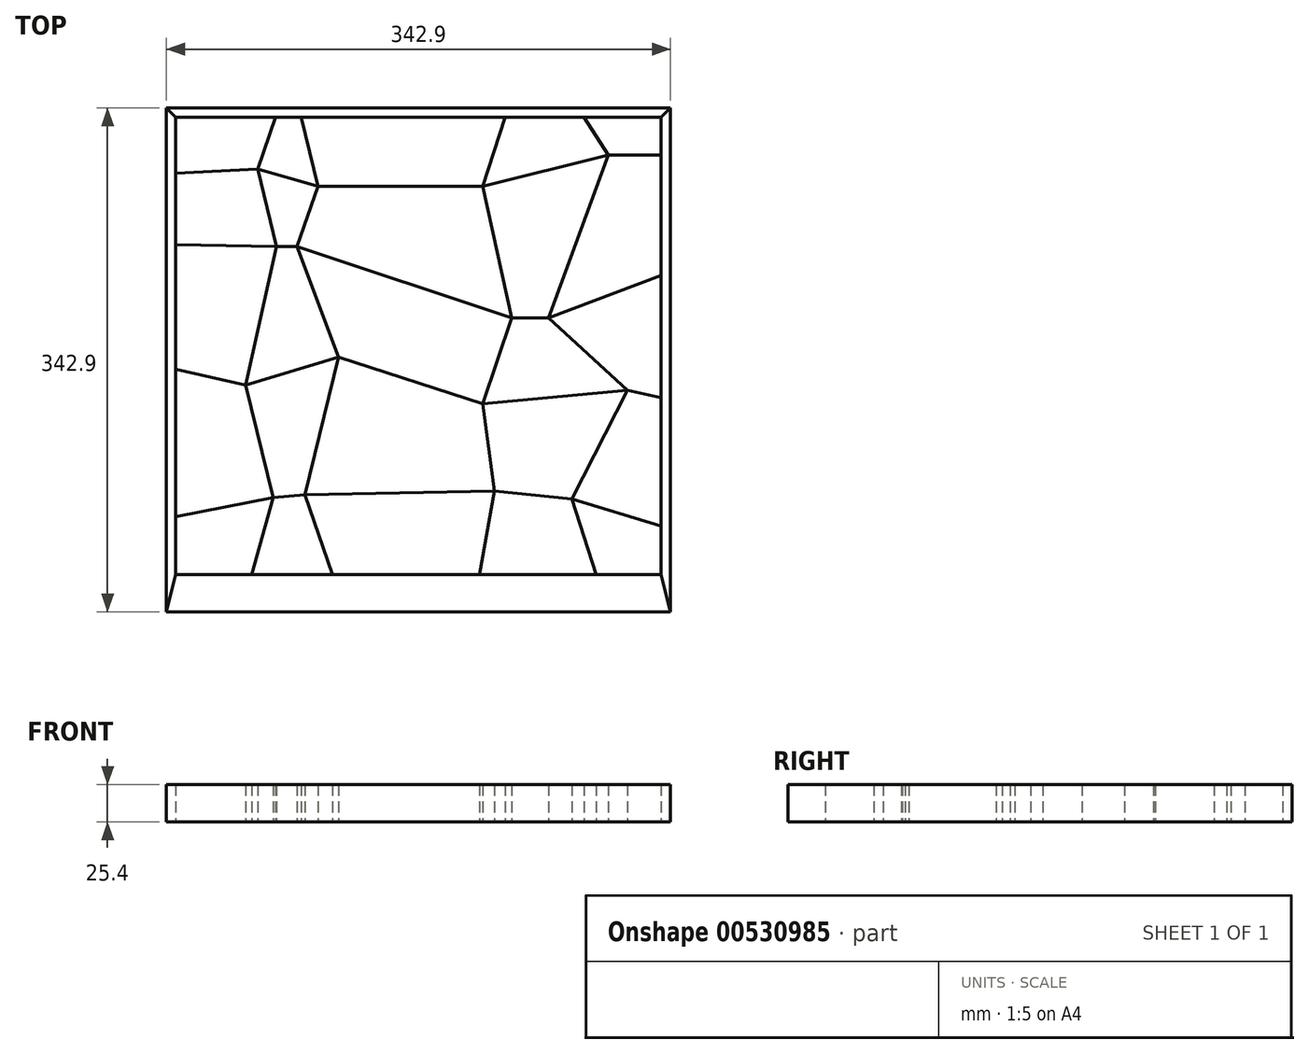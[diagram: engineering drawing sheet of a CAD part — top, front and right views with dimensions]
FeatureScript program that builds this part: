
annotation { "Feature Type Name" : "Feature", "Feature Type Description" : "" }
export const myFeature = defineFeature(function(context is Context, id is Id, definition is map)
    precondition{}
    {
        {
            var Q0;
            Q0=qCreatedBy(makeId("Top.planeOp"),FACE);
            var sketch = newSketch(context, id + "F0", { "sketchPlane" : qUnion([Q0])});
            skLineSegment(sketch, "E0.bottom", {"start": v(171.45, 171.45) * mm, "end": v(-171.45, 171.45) * mm});
            skLineSegment(sketch, "E0.top", {"start": v(171.45, -171.45) * mm, "end": v(-171.45, -171.45) * mm});
            skLineSegment(sketch, "E0.left", {"start": v(171.45, 171.45) * mm, "end": v(171.45, -171.45) * mm});
            skLineSegment(sketch, "E0.right", {"start": v(-171.45, 171.45) * mm, "end": v(-171.45, -171.45) * mm});
            skPoint(sketch, "E0.middle", {"position": v(0, 0) * mm});
            skLineSegment(sketch, "E1.bottom", {"start": v(165.1, 165.1) * mm, "end": v(-165.1, 165.1) * mm});
            skLineSegment(sketch, "E1.top", {"start": v(165.1, -146.05) * mm, "end": v(-165.1, -146.05) * mm});
            skLineSegment(sketch, "E1.left", {"start": v(165.1, 165.1) * mm, "end": v(165.1, -146.05) * mm});
            skLineSegment(sketch, "E1.right", {"start": v(-165.1, 165.1) * mm, "end": v(-165.1, -146.05) * mm});
            skPoint(sketch, "E1.middle", {"position": v(0, 9.53) * mm});
            skLineSegment(sketch, "E2", {"start": v(-165.1, 126.86) * mm, "end": v(-109.46, 129.92) * mm});
            skLineSegment(sketch, "E3", {"start": v(-109.46, 129.92) * mm, "end": v(-96.6, 76.98) * mm});
            skLineSegment(sketch, "E4", {"start": v(-96.6, 76.98) * mm, "end": v(-82.77, 76.98) * mm});
            skLineSegment(sketch, "E5", {"start": v(-82.77, 76.98) * mm, "end": v(-68.32, 118.21) * mm});
            skLineSegment(sketch, "E6", {"start": v(-68.32, 118.21) * mm, "end": v(43.61, 118.21) * mm});
            skLineSegment(sketch, "E7", {"start": v(43.61, 118.21) * mm, "end": v(63.29, 28.59) * mm});
            skLineSegment(sketch, "E8", {"start": v(63.29, 28.59) * mm, "end": v(88.64, 28.59) * mm});
            skLineSegment(sketch, "E9", {"start": v(88.64, 28.59) * mm, "end": v(129.05, 139.32) * mm});
            skLineSegment(sketch, "E10", {"start": v(129.05, 139.32) * mm, "end": v(165.1, 139.32) * mm});
            skLineSegment(sketch, "E11", {"start": v(-109.46, 129.92) * mm, "end": v(-68.32, 118.21) * mm});
            skLineSegment(sketch, "E12", {"start": v(43.61, 118.21) * mm, "end": v(129.05, 139.32) * mm});
            skLineSegment(sketch, "E13", {"start": v(-68.32, 118.21) * mm, "end": v(-79.7, 165.1) * mm});
            skLineSegment(sketch, "E14", {"start": v(-109.46, 129.92) * mm, "end": v(-97.13, 165.1) * mm});
            skLineSegment(sketch, "E15", {"start": v(43.61, 118.21) * mm, "end": v(58.92, 165.1) * mm});
            skLineSegment(sketch, "E16", {"start": v(129.05, 139.32) * mm, "end": v(112.69, 165.1) * mm});
            skLineSegment(sketch, "E17", {"start": v(-165.1, 78.24) * mm, "end": v(-96.6, 76.98) * mm});
            skLineSegment(sketch, "E18", {"start": v(-82.77, 76.98) * mm, "end": v(63.29, 28.59) * mm});
            skLineSegment(sketch, "E19", {"start": v(88.64, 28.59) * mm, "end": v(165.1, 57.3) * mm});
            skLineSegment(sketch, "E20", {"start": v(63.29, 28.59) * mm, "end": v(43.9, -29.94) * mm});
            skLineSegment(sketch, "E21", {"start": v(88.64, 28.59) * mm, "end": v(142.3, -20.55) * mm});
            skLineSegment(sketch, "E22", {"start": v(-82.77, 76.98) * mm, "end": v(-54.36, 1.97) * mm});
            skLineSegment(sketch, "E23", {"start": v(-96.6, 76.98) * mm, "end": v(-117.68, -17.1) * mm});
            skLineSegment(sketch, "E24", {"start": v(-117.68, -17.1) * mm, "end": v(-54.36, 1.97) * mm});
            skLineSegment(sketch, "E25", {"start": v(-54.36, 1.97) * mm, "end": v(43.9, -29.94) * mm});
            skLineSegment(sketch, "E26", {"start": v(43.9, -29.94) * mm, "end": v(142.3, -20.55) * mm});
            skLineSegment(sketch, "E27", {"start": v(142.3, -20.55) * mm, "end": v(165.1, -25.65) * mm});
            skLineSegment(sketch, "E28", {"start": v(-117.68, -17.1) * mm, "end": v(-165.1, -6.49) * mm});
            skLineSegment(sketch, "E29", {"start": v(-117.68, -17.1) * mm, "end": v(-98.74, -93.65) * mm});
            skLineSegment(sketch, "E30", {"start": v(-54.36, 1.97) * mm, "end": v(-77.24, -91.93) * mm});
            skLineSegment(sketch, "E31", {"start": v(43.9, -29.94) * mm, "end": v(51.77, -89.35) * mm});
            skLineSegment(sketch, "E32", {"start": v(142.3, -20.55) * mm, "end": v(104.24, -94.5) * mm});
            skLineSegment(sketch, "E33", {"start": v(-165.1, -106.88) * mm, "end": v(-98.74, -93.65) * mm});
            skLineSegment(sketch, "E34", {"start": v(-98.74, -93.65) * mm, "end": v(-77.24, -91.93) * mm});
            skLineSegment(sketch, "E35", {"start": v(-77.24, -91.93) * mm, "end": v(51.77, -89.35) * mm});
            skLineSegment(sketch, "E36", {"start": v(51.77, -89.35) * mm, "end": v(104.24, -94.5) * mm});
            skLineSegment(sketch, "E37", {"start": v(104.24, -94.5) * mm, "end": v(165.1, -113.22) * mm});
            skLineSegment(sketch, "E38", {"start": v(-98.74, -93.65) * mm, "end": v(-113.3, -146.05) * mm});
            skLineSegment(sketch, "E39", {"start": v(-77.24, -91.93) * mm, "end": v(-58.53, -146.05) * mm});
            skLineSegment(sketch, "E40", {"start": v(51.77, -89.35) * mm, "end": v(41.57, -146.05) * mm});
            skLineSegment(sketch, "E41", {"start": v(104.24, -94.5) * mm, "end": v(120.92, -146.05) * mm});
            skLineSegment(sketch, "E42", {"start": v(-171.45, 171.45) * mm, "end": v(-165.1, 165.1) * mm});
            skLineSegment(sketch, "E43", {"start": v(171.45, 171.45) * mm, "end": v(165.1, 165.1) * mm});
            skLineSegment(sketch, "E44", {"start": v(-165.1, -146.05) * mm, "end": v(-171.45, -171.45) * mm});
            skLineSegment(sketch, "E45", {"start": v(165.1, -146.05) * mm, "end": v(171.45, -171.45) * mm});
            skSolve(sketch);
        }
        {
            var Q0;
            Q0=makeQuery(id+"F0.imprint","IMPRINT",FACE,{"disambiguationData":[TD([[makeQuery(id+"F0.imprint","IMPRINT",EDGE,{"derivedFrom":sQuery(id+"F0.wireOp",EDGE,"E0.bottom")}),1.0]])]});
            var Q1;
            Q1=makeQuery(id+"F0.imprint","IMPRINT",FACE,{"disambiguationData":[TD([[makeQuery(id+"F0.imprint","IMPRINT",EDGE,{"derivedFrom":sQuery(id+"F0.wireOp",EDGE,"E0.top")}),-1.0]])]});
            extrude(context, id + "F1", {"entities" : qUnion([Q0, Q1]), "depth" : 25.4 * mm, "offsetDistance" : 25.4 * mm});
        }
        {
            var Q0;
            Q0=makeQuery(id+"F0.imprint","IMPRINT",FACE,{"disambiguationData":[TD([[makeQuery(id+"F0.imprint","IMPRINT",EDGE,{"derivedFrom":sQuery(id+"F0.wireOp",EDGE,"E0.right")}),1.0]])]});
            var Q1;
            Q1=makeQuery(id+"F0.imprint","IMPRINT",FACE,{"disambiguationData":[TD([[makeQuery(id+"F0.imprint","IMPRINT",EDGE,{"derivedFrom":sQuery(id+"F0.wireOp",EDGE,"E0.left")}),-1.0]])]});
            extrude(context, id + "F2", {"entities" : qUnion([Q0, Q1]), "depth" : 25.4 * mm, "offsetDistance" : 25.4 * mm});
        }
        {
            var Q0;
            Q0=makeQuery(id+"F0.imprint","IMPRINT",FACE,{"disambiguationData":[TD([[makeQuery(id+"F0.imprint","IMPRINT",EDGE,{"derivedFrom":sQuery(id+"F0.wireOp",EDGE,"E11")}),1.0]])]});
            var Q1;
            Q1=makeQuery(id+"F0.imprint","IMPRINT",FACE,{"disambiguationData":[TD([[makeQuery(id+"F0.imprint","IMPRINT",EDGE,{"derivedFrom":sQuery(id+"F0.wireOp",EDGE,"E4")}),-1.0]])]});
            var Q2;
            Q2=makeQuery(id+"F0.imprint","IMPRINT",FACE,{"disambiguationData":[TD([[makeQuery(id+"F0.imprint","IMPRINT",EDGE,{"derivedFrom":sQuery(id+"F0.wireOp",EDGE,"E34")}),-1.0]])]});
            var Q3;
            Q3=makeQuery(id+"F0.imprint","IMPRINT",FACE,{"disambiguationData":[TD([[makeQuery(id+"F0.imprint","IMPRINT",EDGE,{"derivedFrom":sQuery(id+"F0.wireOp",EDGE,"E12")}),1.0]])]});
            var Q4;
            Q4=makeQuery(id+"F0.imprint","IMPRINT",FACE,{"disambiguationData":[TD([[makeQuery(id+"F0.imprint","IMPRINT",EDGE,{"derivedFrom":sQuery(id+"F0.wireOp",EDGE,"E8")}),-1.0]])]});
            var Q5;
            Q5=makeQuery(id+"F0.imprint","IMPRINT",FACE,{"disambiguationData":[TD([[makeQuery(id+"F0.imprint","IMPRINT",EDGE,{"derivedFrom":sQuery(id+"F0.wireOp",EDGE,"E36")}),-1.0]])]});
            extrude(context, id + "F3", {"entities" : qUnion([Q0, Q1, Q2, Q3, Q4, Q5]), "depth" : 25.4 * mm, "offsetDistance" : 25.4 * mm});
        }
        {
            var Q0;
            Q0=makeQuery(id+"F0.imprint","IMPRINT",FACE,{"disambiguationData":[TD([[makeQuery(id+"F0.imprint","IMPRINT",EDGE,{"derivedFrom":sQuery(id+"F0.wireOp",EDGE,"E3")}),1.0]])]});
            var Q1;
            Q1=makeQuery(id+"F0.imprint","IMPRINT",FACE,{"disambiguationData":[TD([[makeQuery(id+"F0.imprint","IMPRINT",EDGE,{"derivedFrom":sQuery(id+"F0.wireOp",EDGE,"E24")}),-1.0]])]});
            var Q2;
            Q2=makeQuery(id+"F0.imprint","IMPRINT",FACE,{"disambiguationData":[TD([[makeQuery(id+"F0.imprint","IMPRINT",EDGE,{"derivedFrom":sQuery(id+"F0.wireOp",EDGE,"E26")}),-1.0]])]});
            var Q3;
            Q3=makeQuery(id+"F0.imprint","IMPRINT",FACE,{"disambiguationData":[TD([[makeQuery(id+"F0.imprint","IMPRINT",EDGE,{"derivedFrom":sQuery(id+"F0.wireOp",EDGE,"E7")}),1.0]])]});
            var Q4;
            Q4=makeQuery(id+"F0.imprint","IMPRINT",FACE,{"disambiguationData":[TD([[makeQuery(id+"F0.imprint","IMPRINT",EDGE,{"derivedFrom":sQuery(id+"F0.wireOp",EDGE,"E6")}),1.0]])]});
            var Q5;
            {var subQ4=sQuery(id+"F0.wireOp",EDGE,"E2");Q5=makeQuery(id+"F0.imprint","IMPRINT",FACE,{"disambiguationData":[TD([[makeQuery(id+"F0.imprint","IMPRINT",EDGE,{"derivedFrom":subQ4}),1.0]])]});}
            var Q6;
            Q6=makeQuery(id+"F0.imprint","IMPRINT",FACE,{"disambiguationData":[TD([[makeQuery(id+"F0.imprint","IMPRINT",EDGE,{"derivedFrom":sQuery(id+"F0.wireOp",EDGE,"E18")}),-1.0]])]});
            var Q7;
            {var subQ0=sQuery(id+"F0.wireOp",EDGE,"E19");Q7=makeQuery(id+"F0.imprint","IMPRINT",FACE,{"disambiguationData":[TD([[makeQuery(id+"F0.imprint","IMPRINT",EDGE,{"derivedFrom":subQ0}),-1.0]])]});}
            var Q8;
            {var subQ4=sQuery(id+"F0.wireOp",EDGE,"E10");Q8=makeQuery(id+"F0.imprint","IMPRINT",FACE,{"disambiguationData":[TD([[makeQuery(id+"F0.imprint","IMPRINT",EDGE,{"derivedFrom":subQ4}),1.0]])]});}
            var Q9;
            {var subQ4=sQuery(id+"F0.wireOp",EDGE,"E37");Q9=makeQuery(id+"F0.imprint","IMPRINT",FACE,{"disambiguationData":[TD([[makeQuery(id+"F0.imprint","IMPRINT",EDGE,{"derivedFrom":subQ4}),-1.0]])]});}
            var Q10;
            Q10=makeQuery(id+"F0.imprint","IMPRINT",FACE,{"disambiguationData":[TD([[makeQuery(id+"F0.imprint","IMPRINT",EDGE,{"derivedFrom":sQuery(id+"F0.wireOp",EDGE,"E35")}),-1.0]])]});
            var Q11;
            {var subQ0=sQuery(id+"F0.wireOp",EDGE,"E17");Q11=makeQuery(id+"F0.imprint","IMPRINT",FACE,{"disambiguationData":[TD([[makeQuery(id+"F0.imprint","IMPRINT",EDGE,{"derivedFrom":subQ0}),-1.0]])]});}
            var Q12;
            {var subQ4=sQuery(id+"F0.wireOp",EDGE,"E33");Q12=makeQuery(id+"F0.imprint","IMPRINT",FACE,{"disambiguationData":[TD([[makeQuery(id+"F0.imprint","IMPRINT",EDGE,{"derivedFrom":subQ4}),-1.0]])]});}
            extrude(context, id + "F4", {"entities" : qUnion([Q0, Q1, Q2, Q3, Q4, Q5, Q6, Q7, Q8, Q9, Q10, Q11, Q12]), "depth" : 25.4 * mm, "offsetDistance" : 25.4 * mm});
        }
        {
            var Q0;
            {var subQ0=sQuery(id+"F0.wireOp",EDGE,"E2");Q0=makeQuery(id+"F0.imprint","IMPRINT",FACE,{"disambiguationData":[TD([[makeQuery(id+"F0.imprint","IMPRINT",EDGE,{"derivedFrom":subQ0}),-1.0]])]});}
            var Q1;
            Q1=makeQuery(id+"F0.imprint","IMPRINT",FACE,{"disambiguationData":[TD([[makeQuery(id+"F0.imprint","IMPRINT",EDGE,{"derivedFrom":sQuery(id+"F0.wireOp",EDGE,"E5")}),-1.0]])]});
            var Q2;
            Q2=makeQuery(id+"F0.imprint","IMPRINT",FACE,{"disambiguationData":[TD([[makeQuery(id+"F0.imprint","IMPRINT",EDGE,{"derivedFrom":sQuery(id+"F0.wireOp",EDGE,"E9")}),-1.0]])]});
            var Q3;
            {var subQ0=sQuery(id+"F0.wireOp",EDGE,"E27");Q3=makeQuery(id+"F0.imprint","IMPRINT",FACE,{"disambiguationData":[TD([[makeQuery(id+"F0.imprint","IMPRINT",EDGE,{"derivedFrom":subQ0}),-1.0]])]});}
            var Q4;
            Q4=makeQuery(id+"F0.imprint","IMPRINT",FACE,{"disambiguationData":[TD([[makeQuery(id+"F0.imprint","IMPRINT",EDGE,{"derivedFrom":sQuery(id+"F0.wireOp",EDGE,"E25")}),-1.0]])]});
            var Q5;
            {var subQ0=sQuery(id+"F0.wireOp",EDGE,"E28");Q5=makeQuery(id+"F0.imprint","IMPRINT",FACE,{"disambiguationData":[TD([[makeQuery(id+"F0.imprint","IMPRINT",EDGE,{"derivedFrom":subQ0}),1.0]])]});}
            extrude(context, id + "F5", {"entities" : qUnion([Q0, Q1, Q2, Q3, Q4, Q5]), "depth" : 25.4 * mm, "offsetDistance" : 25.4 * mm});
        }
    });
